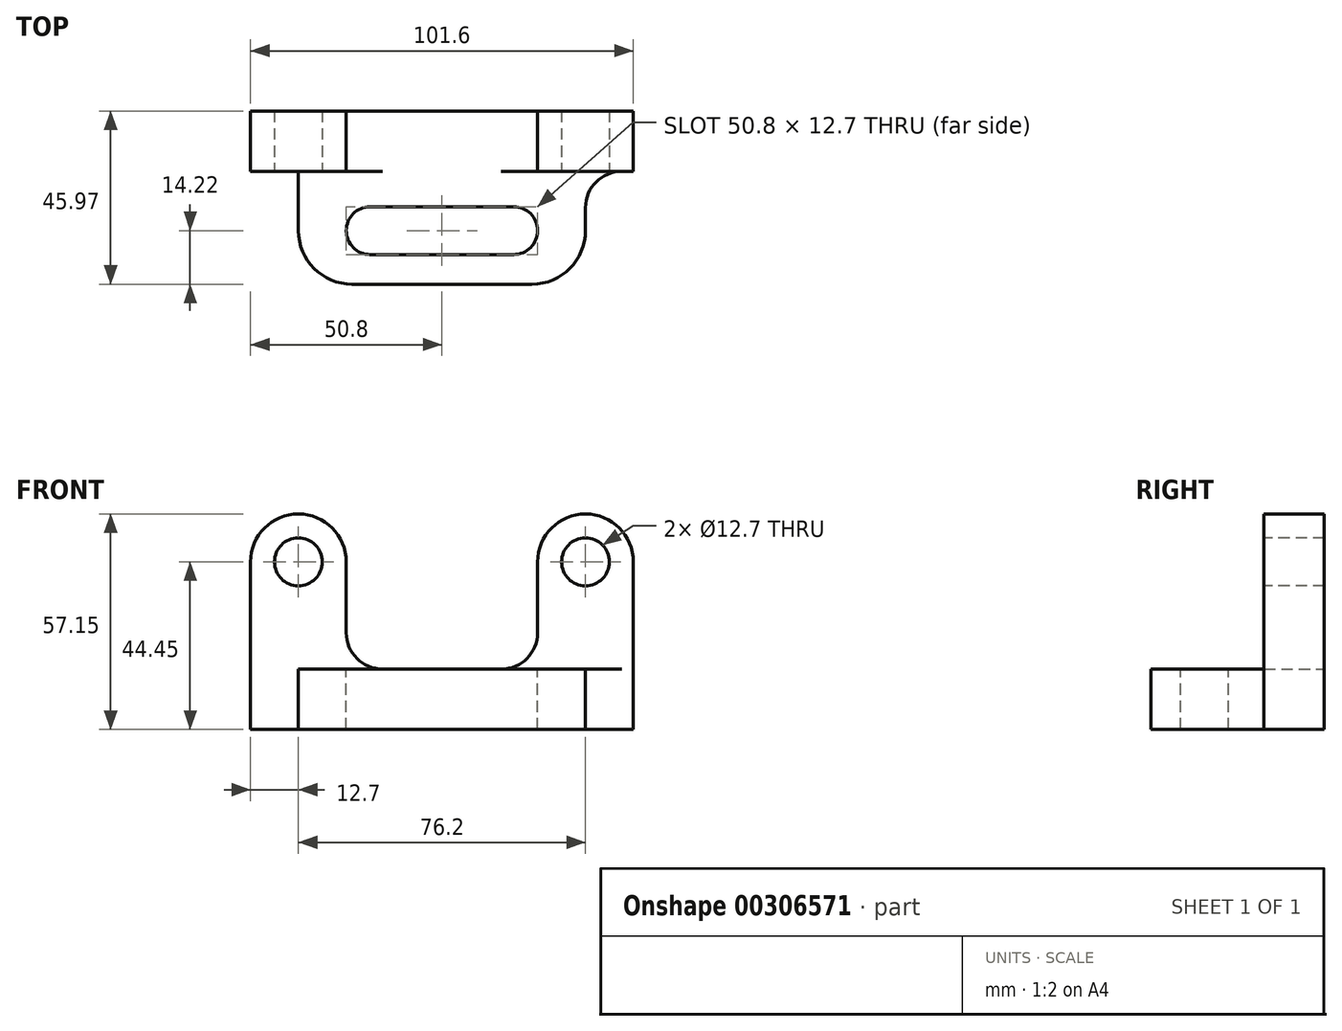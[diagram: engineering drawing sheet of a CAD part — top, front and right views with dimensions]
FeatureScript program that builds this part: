
annotation { "Feature Type Name" : "Feature", "Feature Type Description" : "" }
export const myFeature = defineFeature(function(context is Context, id is Id, definition is map)
    precondition{}
    {
        {
            var Q0;
            Q0=qCreatedBy(makeId("Front.planeOp"),FACE);
            var sketch = newSketch(context, id + "F0", { "sketchPlane" : qUnion([Q0])});
            skLineSegment(sketch, "E0", {"start": v(0, 0) * mm, "end": v(0, 44.45) * mm});
            skLineSegment(sketch, "E1", {"start": v(0, 0) * mm, "end": v(101.6, 0) * mm});
            skLineSegment(sketch, "E2", {"start": v(101.6, 0) * mm, "end": v(101.6, 44.45) * mm});
            skArc(sketch, "E3", {"start": v(101.6, 44.45) * mm, "mid": v(88.9, 57.15) * mm, "end": v(76.2, 44.45) * mm});
            skArc(sketch, "E4", {"start": v(0, 44.45) * mm, "mid": v(12.7, 57.15) * mm, "end": v(25.4, 44.45) * mm});
            skLineSegment(sketch, "E5", {"start": v(25.4, 16) * mm, "end": v(76.2, 16) * mm});
            skLineSegment(sketch, "E6", {"start": v(76.2, 44.45) * mm, "end": v(76.2, 16) * mm});
            skLineSegment(sketch, "E7", {"start": v(25.4, 44.45) * mm, "end": v(25.4, 16) * mm});
            skSolve(sketch);
        }
        {
            var Q0;
            Q0 = qSketchRegion(id + "F0", true);
            extrude(context, id + "F1", {"entities" : qUnion([Q0]), "depth" : 16 * mm});
        }
        {
            var Q0;
            Q0=makeQuery(id+"F1.opExtrude","SWEPT_EDGE",EDGE,{"disambiguationData":[OSD([sQuery(id+"F0.wireOp",EDGE,"E5"),sQuery(id+"F0.wireOp",EDGE,"E7")])]});
            var Q1;
            Q1=makeQuery(id+"F1.opExtrude","SWEPT_EDGE",EDGE,{"disambiguationData":[OSD([sQuery(id+"F0.wireOp",EDGE,"E5"),sQuery(id+"F0.wireOp",EDGE,"E6")])]});
            fillet(context, id + "F2", {"entities" : qUnion([Q0, Q1]), "radius" : 9.65 * mm, "tangentPropagation" : true, "allowEdgeOverflow" : false});
        }
        {
            var Q0;
            Q0=qCreatedBy(makeId("Top.planeOp"),FACE);
            var sketch = newSketch(context, id + "F3", { "sketchPlane" : qUnion([Q0])});
            skLineSegment(sketch, "E8.bottom", {"start": v(12.7, -16) * mm, "end": v(88.9, -16) * mm});
            skLineSegment(sketch, "E8.top", {"start": v(12.7, -45.97) * mm, "end": v(88.9, -45.97) * mm});
            skLineSegment(sketch, "E8.left", {"start": v(12.7, -16) * mm, "end": v(12.7, -45.97) * mm});
            skLineSegment(sketch, "E8.right", {"start": v(88.9, -16) * mm, "end": v(88.9, -45.97) * mm});
            skSolve(sketch);
        }
        {
            var Q0;
            Q0 = qSketchRegion(id + "F3", true);
            extrude(context, id + "F4", {"entities" : qUnion([Q0]), "operationType" : NewBodyOperationType.ADD, "depth" : 16 * mm});
        }
        {
            var Q0;
            Q0=makeQuery(id+"F4.opExtrude","SWEPT_EDGE",EDGE,{"disambiguationData":[OSD([sQuery(id+"F3.wireOp",EDGE,"E8.top"),sQuery(id+"F3.wireOp",EDGE,"E8.right")])]});
            var Q1;
            Q1=makeQuery(id+"F4.opExtrude","SWEPT_EDGE",EDGE,{"disambiguationData":[OSD([sQuery(id+"F3.wireOp",EDGE,"E8.top"),sQuery(id+"F3.wireOp",EDGE,"E8.left")])]});
            fillet(context, id + "F5", {"entities" : qUnion([Q0, Q1]), "radius" : 14.22 * mm, "tangentPropagation" : true, "allowEdgeOverflow" : false});
        }
        {
            var Q0;
            Q0=makeQuery(id+"F4.opExtrude","SWEPT_EDGE",EDGE,{"disambiguationData":[OSD([sQuery(id+"F3.wireOp",EDGE,"E8.bottom"),sQuery(id+"F3.wireOp",EDGE,"E8.right")])]});
            var Q1;
            Q1=makeQuery(id+"F4.opExtrude","SWEPT_EDGE",EDGE,{"disambiguationData":[OSD([sQuery(id+"F3.wireOp",EDGE,"E8.bottom"),sQuery(id+"F3.wireOp",EDGE,"E8.left")])]});
            fillet(context, id + "F6", {"entities" : qUnion([Q0, Q1]), "radius" : 9.65 * mm, "tangentPropagation" : true, "allowEdgeOverflow" : false});
        }
        {
            var Q0;
            {var subQ0=sQuery(id+"F0.wireOp",EDGE,"E5");var subQ5=sQuery(id+"F0.wireOp",EDGE,"E4");var subQ6=sQuery(id+"F0.wireOp",EDGE,"E1");var subQ7=sQuery(id+"F0.wireOp",EDGE,"E0");var subQ8=sQuery(id+"F0.wireOp",EDGE,"E7");Q0=makeQuery(id+"F4.boolean.opBoolean","SPLIT",FACE,{"disambiguationData":[TD([makeQuery(id+"F1.opExtrude","SWEPT_FACE",FACE,{"disambiguationData":[OSD([subQ7])]})])],"derivedFrom":makeQuery(id+"F1.opExtrude","CAP_FACE",FACE,{"disambiguationData":[OSD([subQ7,subQ6,sQuery(id+"F0.wireOp",EDGE,"E2"),sQuery(id+"F0.wireOp",EDGE,"E3"),subQ5,subQ0,sQuery(id+"F0.wireOp",EDGE,"E6"),subQ8])],"isStart":false})});}
            var sketch = newSketch(context, id + "F7", { "sketchPlane" : qUnion([Q0])});
            skCircle(sketch, "E9", {"center": v(12.7, 44.45) * mm, "radius": 6.35 * mm});
            skCircle(sketch, "E10", {"center": v(88.9, 44.45) * mm, "radius": 6.35 * mm});
            skSolve(sketch);
        }
        {
            var Q0;
            Q0 = qSketchRegion(id + "F7", true);
            extrude(context, id + "F8", {"entities" : qUnion([Q0]), "operationType" : NewBodyOperationType.REMOVE, "endBound" : BoundingType.THROUGH_ALL, "oppositeDirection" : true, "depth" : 25.4 * mm});
        }
        {
            var Q0;
            Q0=makeQuery(id+"F4.boolean.opBoolean","MERGE",FACE,{"derivedFrom":[makeQuery(id+"F1.opExtrude","SWEPT_FACE",FACE,{"disambiguationData":[OSD([sQuery(id+"F0.wireOp",EDGE,"E5")])]}),makeQuery(id+"F4.opExtrude","CAP_FACE",FACE,{"disambiguationData":[OSD([sQuery(id+"F3.wireOp",EDGE,"E8.bottom"),sQuery(id+"F3.wireOp",EDGE,"E8.top"),sQuery(id+"F3.wireOp",EDGE,"E8.left"),sQuery(id+"F3.wireOp",EDGE,"E8.right")])],"isStart":false})]});
            var sketch = newSketch(context, id + "F9", { "sketchPlane" : qUnion([Q0])});
            skLineSegment(sketch, "E11", {"start": v(18.78, -31.75) * mm, "end": v(69.85, -31.75) * mm, "construction": true});
            skLineSegment(sketch, "E12", {"start": v(31.75, -25.4) * mm, "end": v(69.85, -25.4) * mm});
            skArc(sketch, "E13", {"start": v(31.75, -25.4) * mm, "mid": v(25.4, -31.75) * mm, "end": v(31.75, -38.1) * mm});
            skArc(sketch, "E14", {"start": v(69.85, -25.4) * mm, "mid": v(76.2, -31.75) * mm, "end": v(69.85, -38.1) * mm});
            skLineSegment(sketch, "E15", {"start": v(31.75, -38.1) * mm, "end": v(69.85, -38.1) * mm});
            skSolve(sketch);
        }
        {
            var Q0;
            Q0 = qSketchRegion(id + "F9", true);
            extrude(context, id + "F10", {"entities" : qUnion([Q0]), "operationType" : NewBodyOperationType.REMOVE, "endBound" : BoundingType.THROUGH_ALL, "oppositeDirection" : true, "depth" : 25.4 * mm});
        }
    });
